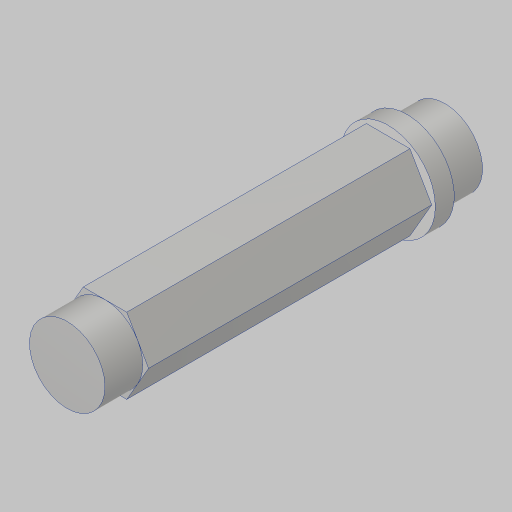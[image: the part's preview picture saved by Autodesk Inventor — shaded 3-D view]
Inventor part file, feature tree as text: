
AUTODESK INVENTOR PART (.ipt)
format: ipt  version: 2023.5 (Build 275446000, 446)  size: 146,944 bytes
history: native  units: in
note: dims shown in document units (in); Inventor stores cm internally (conversion verified against a paired STEP export)
features: extrude x5, sketch x5, projected_geometry x4
ambient origin geometry x8: Origin, YZ Plane, XZ Plane, XY Plane, X Axis, Y Axis, Z Axis, Center Point
bodies: Solid1 (feature_tree)
feature tree (14):
  extrude  "Extrusion1"  Depth=3.5625in TaperAngle=0.0deg
  extrude  "Extrusion2"  Depth=2.125in TaperAngle=0.0deg
  extrude  "Extrusion3"  Depth=0.25in TaperAngle=0.0deg
  extrude  "Extrusion4"  TaperAngle=0.0deg  [1 undecoded]
  extrude  "Extrusion5"  Depth=0.25in TaperAngle=0.0deg
  sketch  "Sketch1"  dims[d0=0.625in d1=3.5625in d2=0.0in]
  sketch  "Sketch2"  dims[d3=0.5in d4=2.125in d5=0.0in]
  projected_geometry  "Projected Loop1"
  sketch  "Sketch3"  dims[d6=0.5in d7=0.25in d8=0.0in]
  projected_geometry  "Projected Loop2"
  sketch  "Sketch4"  dims[d9=2.5in d10=0.0in d11=0.0in]
  sketch  "Sketch5"  dims[d12=0.5in d13=0.25in d14=0.0in]
  projected_geometry  "Project Cut Edges1"
  projected_geometry  "Project Cut Edges2"
note: 1 required parameter value undecoded (feature->parameter linkage not recoverable at this tier; creation-order binding heuristic only, values carry confidence <= 0.55)
